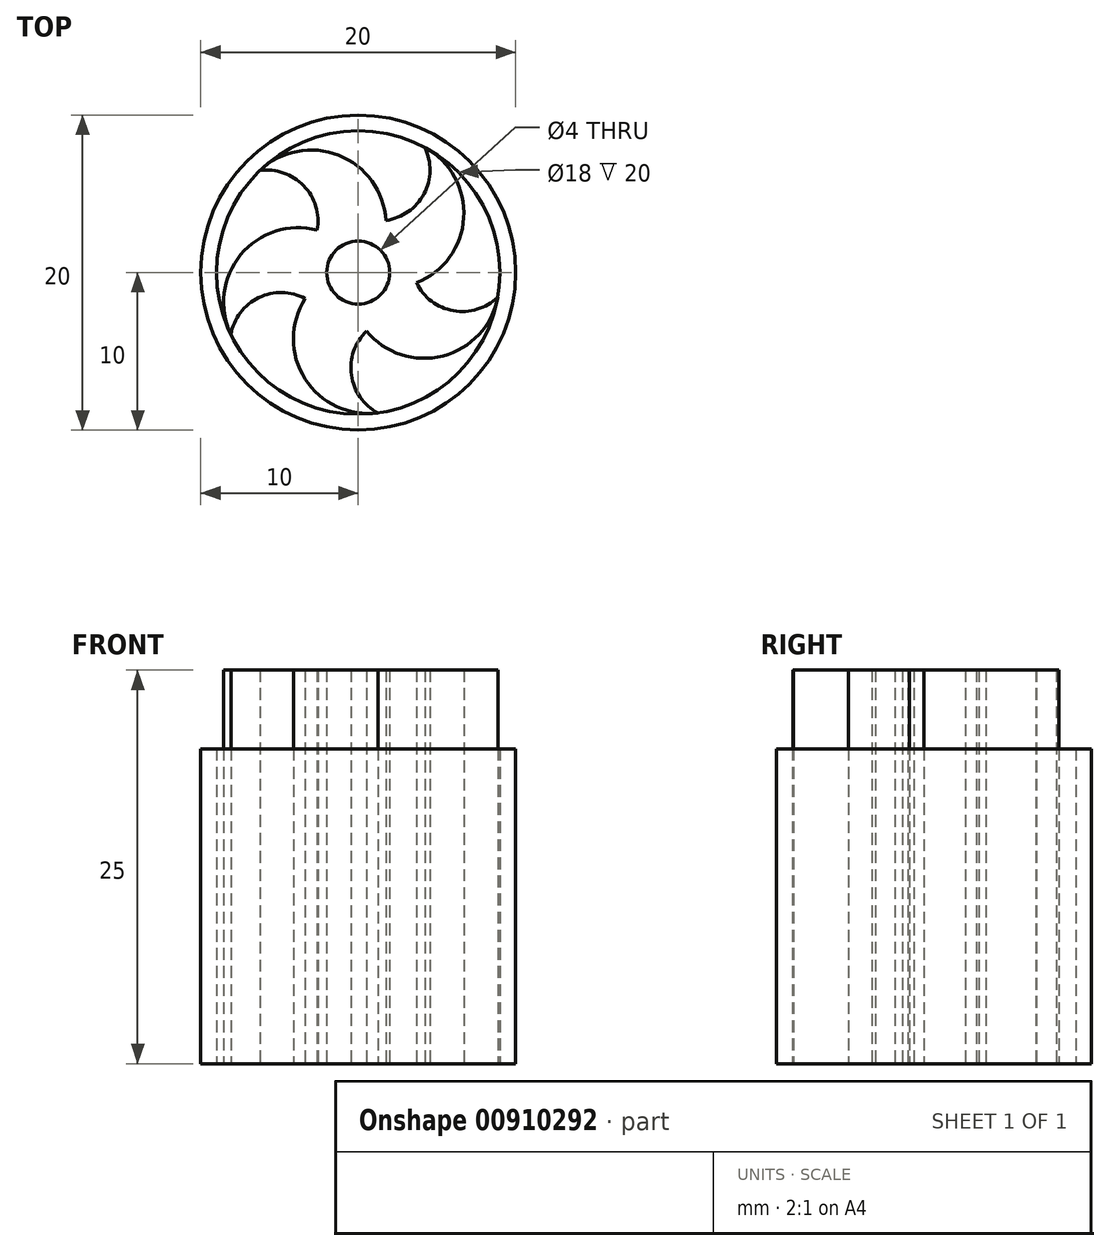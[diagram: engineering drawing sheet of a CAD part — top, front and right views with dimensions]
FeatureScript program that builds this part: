
annotation { "Feature Type Name" : "Feature", "Feature Type Description" : "" }
export const myFeature = defineFeature(function(context is Context, id is Id, definition is map)
    precondition{}
    {
        {
            var Q0;
            Q0=qCreatedBy(makeId("Top.planeOp"),FACE);
            var sketch = newSketch(context, id + "F0", { "sketchPlane" : qUnion([Q0])});
            skCircle(sketch, "E0", {"center": v(0, 0) * mm, "radius": 10 * mm});
            skCircle(sketch, "E1", {"center": v(0, 0) * mm, "radius": 9 * mm});
            skSolve(sketch);
        }
        {
            var Q0;
            Q0=makeQuery(id+"F0.imprint","IMPRINT",FACE,{"disambiguationData":[TD([[makeQuery(id+"F0.imprint","IMPRINT",EDGE,{"derivedFrom":sQuery(id+"F0.wireOp",EDGE,"E0")}),1.0]])]});
            extrude(context, id + "F1", {"entities" : qUnion([Q0]), "depth" : 20 * mm, "offsetDistance" : 25 * mm});
        }
        {
            var Q0;
            Q0=qCreatedBy(makeId("Top.planeOp"),FACE);
            var sketch = newSketch(context, id + "F2", { "sketchPlane" : qUnion([Q0])});
            skLineSegment(sketch, "E2.0", {"start": v(0.52, -3.71) * mm, "end": v(-3.37, -1.64) * mm});
            skLineSegment(sketch, "E2.1", {"start": v(-3.37, -1.64) * mm, "end": v(-2.6, 2.7) * mm});
            skLineSegment(sketch, "E2.2", {"start": v(-2.6, 2.7) * mm, "end": v(1.76, 3.31) * mm});
            skLineSegment(sketch, "E2.3", {"start": v(1.76, 3.31) * mm, "end": v(3.7, -0.65) * mm});
            skLineSegment(sketch, "E2.4", {"start": v(3.7, -0.65) * mm, "end": v(0.52, -3.71) * mm});
            skPoint(sketch, "E3", {"position": v(0, 0) * mm});
            skArc(sketch, "E4", {"start": v(3.7, -0.65) * mm, "mid": v(6.05, -2.43) * mm, "end": v(8.86, -1.56) * mm});
            skArc(sketch, "E5", {"start": v(1.76, 3.31) * mm, "mid": v(4.17, 5) * mm, "end": v(4.23, 7.95) * mm});
            skArc(sketch, "E6", {"start": v(-2.6, 2.7) * mm, "mid": v(-3.47, 5.52) * mm, "end": v(-6.25, 6.47) * mm});
            skArc(sketch, "E7", {"start": v(-3.37, -1.64) * mm, "mid": v(-6.32, -1.6) * mm, "end": v(-8.09, -3.94) * mm});
            skArc(sketch, "E8", {"start": v(-2.6, 2.7) * mm, "mid": v(-7.47, 1.13) * mm, "end": v(-8.09, -3.94) * mm});
            skArc(sketch, "E9", {"start": v(1.76, 3.31) * mm, "mid": v(-1.24, 7.45) * mm, "end": v(-6.25, 6.47) * mm});
            skArc(sketch, "E10", {"start": v(3.7, -0.65) * mm, "mid": v(6.7, 3.48) * mm, "end": v(4.23, 7.95) * mm});
            skArc(sketch, "E11", {"start": v(0.52, -3.71) * mm, "mid": v(5.38, -5.3) * mm, "end": v(8.86, -1.56) * mm});
            skArc(sketch, "E12", {"start": v(-3.37, -1.64) * mm, "mid": v(-3.38, -6.75) * mm, "end": v(1.25, -8.91) * mm});
            skArc(sketch, "E13", {"start": v(0.52, -3.71) * mm, "mid": v(-0.44, -6.5) * mm, "end": v(1.25, -8.91) * mm});
            skCircle(sketch, "E14", {"center": v(0, 0) * mm, "radius": 2 * mm});
            skSolve(sketch);
        }
        {
            var Q0;
            Q0=makeQuery(id+"F2.imprint","IMPRINT",FACE,{"disambiguationData":[TD([[makeQuery(id+"F2.imprint","IMPRINT",EDGE,{"derivedFrom":sQuery(id+"F2.wireOp",EDGE,"E2.4")}),1.0]])]});
            var Q1;
            Q1=makeQuery(id+"F2.imprint","IMPRINT",FACE,{"disambiguationData":[TD([[makeQuery(id+"F2.imprint","IMPRINT",EDGE,{"derivedFrom":sQuery(id+"F2.wireOp",EDGE,"E2.0")}),-1.0]])]});
            var Q2;
            Q2=makeQuery(id+"F2.imprint","IMPRINT",FACE,{"disambiguationData":[TD([[makeQuery(id+"F2.imprint","IMPRINT",EDGE,{"derivedFrom":sQuery(id+"F2.wireOp",EDGE,"E2.2")}),1.0]])]});
            var Q3;
            Q3=makeQuery(id+"F2.imprint","IMPRINT",FACE,{"disambiguationData":[TD([[makeQuery(id+"F2.imprint","IMPRINT",EDGE,{"derivedFrom":sQuery(id+"F2.wireOp",EDGE,"E2.3")}),1.0]])]});
            var Q4;
            Q4=makeQuery(id+"F2.imprint","IMPRINT",FACE,{"disambiguationData":[TD([[makeQuery(id+"F2.imprint","IMPRINT",EDGE,{"derivedFrom":sQuery(id+"F2.wireOp",EDGE,"E2.1")}),1.0]])]});
            var Q5;
            Q5=makeQuery(id+"F2.imprint","IMPRINT",FACE,{"disambiguationData":[TD([[makeQuery(id+"F2.imprint","IMPRINT",EDGE,{"derivedFrom":sQuery(id+"F2.wireOp",EDGE,"E2.0")}),1.0]])]});
            extrude(context, id + "F3", {"entities" : qUnion([Q0, Q1, Q2, Q3, Q4, Q5]), "depth" : 25 * mm, "offsetDistance" : 25 * mm});
        }
    });
